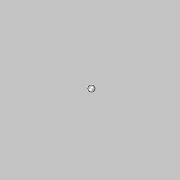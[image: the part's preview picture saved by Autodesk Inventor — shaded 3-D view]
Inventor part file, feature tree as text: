
AUTODESK INVENTOR PART (.ipt)
format: ipt  version: 2017 (Build 210142000, 142)  size: 131,072 bytes
history: native  units: mm
features: other x39, extrude x4, sketch x2, projected_geometry x2, plane x1
ambient origin geometry x7: Origin, YZ Plane, XZ Plane, X Axis, Y Axis, Z Axis, Center Point
bodies: Solid1 (feature_tree)
feature tree (48):
  other  "Table"
  other  "HangingElectricalCabinet300x200x120mm1Door"
  other  "HangingElectricalCabinet300x200x155mm1Door"
  other  "HangingElectricalCabinet300x300x155mm1Door"
  other  "HangingElectricalCabinet300x300x210mm1Door"
  other  "HangingElectricalCabinet380x300x210mm1Door"
  other  "HangingElectricalCabinet400x300x210mm1Door"
  other  "HangingElectricalCabinet300x380x155mm1Door"
  other  "HangingElectricalCabinet300x380x210mm1Door"
  other  "HangingElectricalCabinet380x380x210mm1Door"
  other  "HangingElectricalCabinet600x380x210mm1Door"
  other  "HangingElectricalCabinet600x380x350mm1Door"
  other  "HangingElectricalCabinet500x400x210mm1Door"
  other  "HangingElectricalCabinet800x400x300mm1Door"
  other  "HangingElectricalCabinet500x500x210mm1Door"
  other  "HangingElectricalCabinet500x500x300mm1Door"
  other  "HangingElectricalCabinet700x500x250mm1Door"
  other  "HangingElectricalCabinet380x600x210mm1Door"
  other  "HangingElectricalCabinet380x600x350mm1Door"
  other  "HangingElectricalCabinet600x600x210mm1Door"
  other  "HangingElectricalCabinet600x600x250mm1Door"
  other  "HangingElectricalCabinet600x600x350mm1Door"
  other  "HangingElectricalCabinet760x600x210mm1Door"
  other  "HangingElectricalCabinet760x600x350mm1Door"
  other  "HangingElectricalCabinet800x600x250mm1Door"
  other  "HangingElectricalCabinet1000x600x250mm1Door"
  other  "HangingElectricalCabinet1200x600x300mm1Door"
  other  "HangingElectricalCabinet760x760x210mm1Door"
  other  "HangingElectricalCabinet760x760x300mm1Door"
  other  "HangingElectricalCabinet600x800x300mm1Door"
  other  "HangingElectricalCabinet1000x800x300mm1Door"
  other  "HangingElectricalCabinet1200x800x300mm1Door"
  other  "HangingElectricalCabinet760x1000x210mm2Doors"
  other  "HangingElectricalCabinet760x1000x300mm2Doors"
  other  "HangingElectricalCabinet1000x1000x300mm2Doors"
  other  "HangingElectricalCabinet1200x1000x300mm2Doors"
  other  "HangingElectricalCabinet1400x1000x300mm2Doors"
  other  "FirstSketch"
  extrude  "Extrusion1"  TaperAngle=0.0deg  [1 undecoded]
  extrude  "Extrusion2"  TaperAngle=0.0deg  [1 undecoded]
  extrude  "Extrusion3"  Depth=2.0mm
  plane  "Work Plane2"
  extrude  "Extrusion5"  Depth=20.0mm TaperAngle=0.0deg
  other  "XY Ground Plane"
  sketch  "Sketch4"  dims[d3=10.0mm d6=0.0mm]
  projected_geometry  "Projected Loop1"
  sketch  "Sketch7"  dims[d7=200.0mm d8=0.0mm d9=2.0mm d10=20.0mm d11=0.0mm d21=5.0mm d22=20.0mm d23=0.0mm d24=10.0mm d25=0.0mm]
  projected_geometry  "Projected Loop2"
note: 2 required parameter values undecoded (feature->parameter linkage not recoverable at this tier; creation-order binding heuristic only, values carry confidence <= 0.55)
